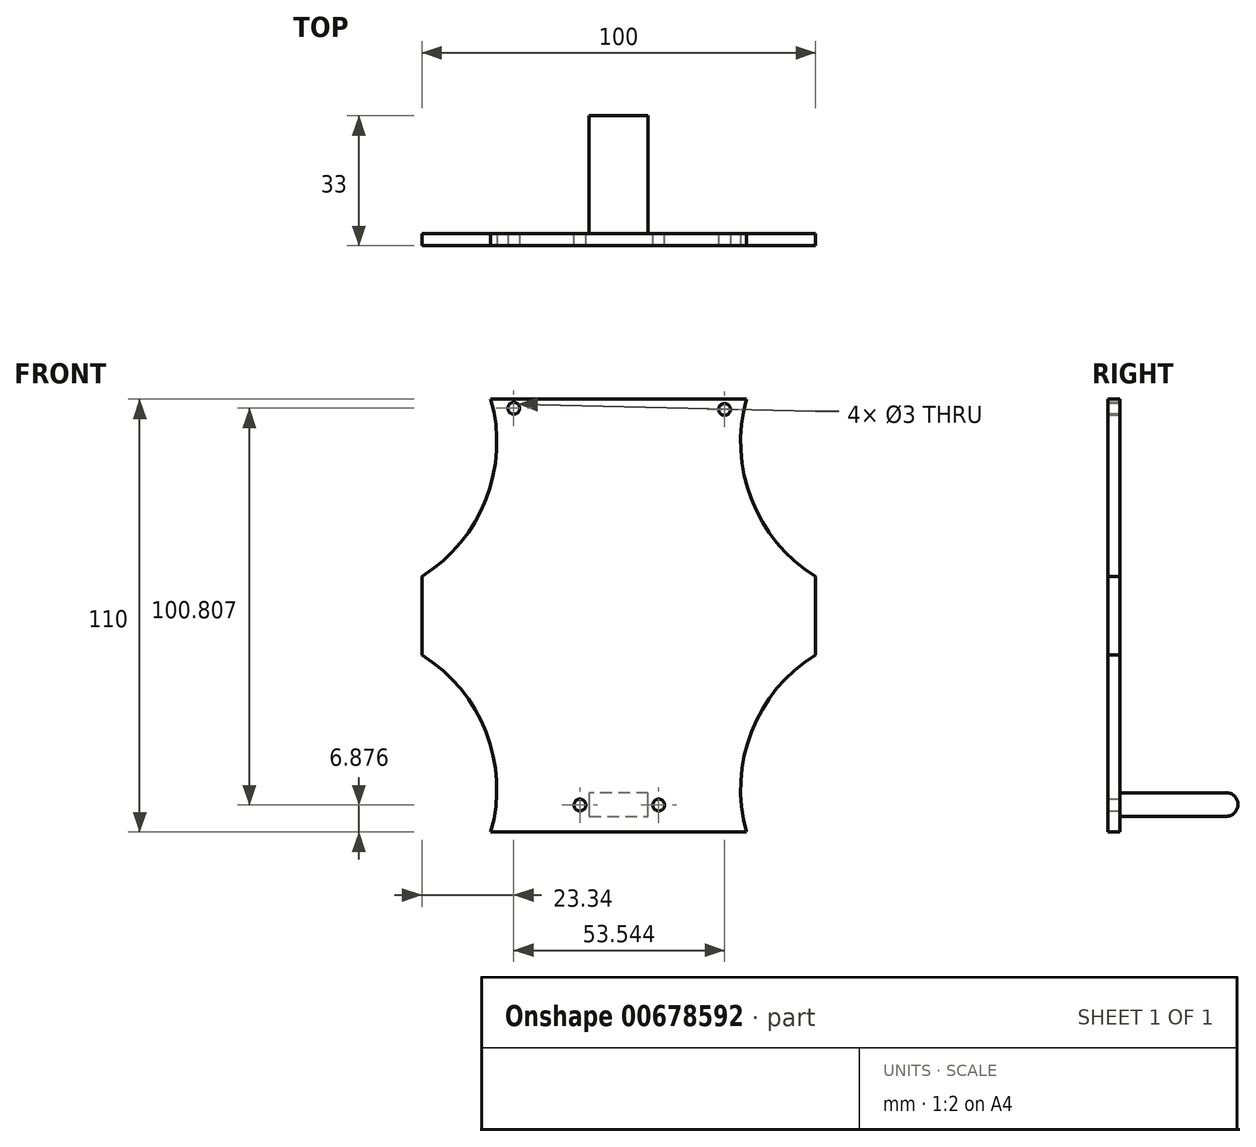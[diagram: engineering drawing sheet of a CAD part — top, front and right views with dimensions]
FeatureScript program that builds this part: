
annotation { "Feature Type Name" : "Feature", "Feature Type Description" : "" }
export const myFeature = defineFeature(function(context is Context, id is Id, definition is map)
    precondition{}
    {
        {
            var Q0;
            Q0=qCreatedBy(makeId("Front.planeOp"),FACE);
            var sketch = newSketch(context, id + "F0", { "sketchPlane" : qUnion([Q0])});
            skLineSegment(sketch, "E0.bottom", {"start": v(0, 0) * mm, "end": v(100, 0) * mm});
            skLineSegment(sketch, "E0.top", {"start": v(0, 110) * mm, "end": v(100, 110) * mm});
            skLineSegment(sketch, "E0.left", {"start": v(0, 0) * mm, "end": v(0, 110) * mm});
            skLineSegment(sketch, "E0.right", {"start": v(100, 0) * mm, "end": v(100, 110) * mm});
            skSolve(sketch);
        }
        {
            var Q0;
            Q0=makeQuery(id+"F0.imprint","IMPRINT",FACE,{"disambiguationData":[TD([[makeQuery(id+"F0.imprint","IMPRINT",EDGE,{"derivedFrom":sQuery(id+"F0.wireOp",EDGE,"E0.bottom")}),1.0]])]});
            extrude(context, id + "F1", {"entities" : qUnion([Q0]), "depth" : 3 * mm, "offsetDistance" : 25 * mm});
        }
        {
            var Q0;
            Q0=makeQuery(id+"F1.opExtrude","CAP_FACE",FACE,{"disambiguationData":[OSD([sQuery(id+"F0.wireOp",EDGE,"E0.bottom"),sQuery(id+"F0.wireOp",EDGE,"E0.top"),sQuery(id+"F0.wireOp",EDGE,"E0.left"),sQuery(id+"F0.wireOp",EDGE,"E0.right")])],"isStart":false});
            var sketch = newSketch(context, id + "F2", { "sketchPlane" : qUnion([Q0])});
            skLineSegment(sketch, "E1", {"start": v(0, 0) * mm, "end": v(0, 45) * mm});
            skLineSegment(sketch, "E2", {"start": v(0, 110) * mm, "end": v(0, 65) * mm});
            skLineSegment(sketch, "E3", {"start": v(100, 110) * mm, "end": v(100, 65) * mm});
            skLineSegment(sketch, "E4", {"start": v(100, 0) * mm, "end": v(100, 45) * mm});
            skLineSegment(sketch, "E5", {"start": v(0, 0) * mm, "end": v(17.5, 0) * mm});
            skLineSegment(sketch, "E6", {"start": v(100, 0) * mm, "end": v(82.5, 0) * mm});
            skLineSegment(sketch, "E7", {"start": v(0, 110) * mm, "end": v(17.5, 110) * mm});
            skLineSegment(sketch, "E8", {"start": v(100, 110) * mm, "end": v(82.5, 110) * mm});
            skArc(sketch, "E9", {"start": v(0, 65) * mm, "mid": v(16.3, 84.56) * mm, "end": v(17.5, 110) * mm});
            skArc(sketch, "E10", {"start": v(82.5, 110) * mm, "mid": v(83.7, 84.56) * mm, "end": v(100, 65) * mm});
            skArc(sketch, "E11", {"start": v(100, 45) * mm, "mid": v(83.7, 25.44) * mm, "end": v(82.5, 0) * mm});
            skArc(sketch, "E12", {"start": v(17.5, 0) * mm, "mid": v(16.3, 25.44) * mm, "end": v(0, 45) * mm});
            skSolve(sketch);
        }
        {
            var Q0;
            Q0=makeQuery(id+"F2.imprint","IMPRINT",FACE,{"disambiguationData":[TD([[makeQuery(id+"F2.imprint","IMPRINT",EDGE,{"derivedFrom":sQuery(id+"F2.wireOp",EDGE,"E2")}),-1.0]])]});
            var Q1;
            Q1=makeQuery(id+"F2.imprint","IMPRINT",FACE,{"disambiguationData":[TD([[makeQuery(id+"F2.imprint","IMPRINT",EDGE,{"derivedFrom":sQuery(id+"F2.wireOp",EDGE,"E3")}),1.0]])]});
            var Q2;
            Q2=makeQuery(id+"F2.imprint","IMPRINT",FACE,{"disambiguationData":[TD([[makeQuery(id+"F2.imprint","IMPRINT",EDGE,{"derivedFrom":sQuery(id+"F2.wireOp",EDGE,"E4")}),1.0]])]});
            var Q3;
            Q3=makeQuery(id+"F2.imprint","IMPRINT",FACE,{"disambiguationData":[TD([[makeQuery(id+"F2.imprint","IMPRINT",EDGE,{"derivedFrom":sQuery(id+"F2.wireOp",EDGE,"E1")}),-1.0]])]});
            extrude(context, id + "F3", {"entities" : qUnion([Q0, Q1, Q2, Q3]), "operationType" : NewBodyOperationType.REMOVE, "oppositeDirection" : true, "depth" : 25 * mm, "offsetDistance" : 25 * mm});
        }
        {
            var Q0;
            Q0=makeQuery(id+"F1.opExtrude","CAP_FACE",FACE,{"disambiguationData":[OSD([sQuery(id+"F0.wireOp",EDGE,"E0.bottom"),sQuery(id+"F0.wireOp",EDGE,"E0.top"),sQuery(id+"F0.wireOp",EDGE,"E0.left"),sQuery(id+"F0.wireOp",EDGE,"E0.right")])],"isStart":true});
            var sketch = newSketch(context, id + "F4", { "sketchPlane" : qUnion([Q0])});
            skLineSegment(sketch, "E13", {"start": v(-82.5, 0) * mm, "end": v(-57.5, 0) * mm});
            skLineSegment(sketch, "E14", {"start": v(-17.5, 0) * mm, "end": v(-42.5, 0) * mm});
            skLineSegment(sketch, "E15", {"start": v(-42.5, 4) * mm, "end": v(-57.5, 4) * mm});
            skLineSegment(sketch, "E16", {"start": v(-57.5, 4) * mm, "end": v(-57.5, 10) * mm});
            skLineSegment(sketch, "E17", {"start": v(-57.5, 10) * mm, "end": v(-42.5, 10) * mm});
            skLineSegment(sketch, "E18", {"start": v(-42.5, 10) * mm, "end": v(-42.5, 4) * mm});
            skSolve(sketch);
        }
        {
            var Q0;
            Q0=makeQuery(id+"F4.imprint","IMPRINT",FACE,{"disambiguationData":[TD([[makeQuery(id+"F4.imprint","IMPRINT",EDGE,{"derivedFrom":sQuery(id+"F4.wireOp",EDGE,"E15")}),-1.0]])]});
            extrude(context, id + "F5", {"entities" : qUnion([Q0]), "operationType" : NewBodyOperationType.ADD, "depth" : 30 * mm, "offsetDistance" : 25 * mm});
        }
        {
            var Q0;
            Q0=makeQuery(id+"F5.opExtrude","CAP_EDGE",EDGE,{"disambiguationData":[OSD([sQuery(id+"F4.wireOp",EDGE,"E15")])],"isStart":false});
            fillet(context, id + "F6", {"entities" : qUnion([Q0]), "radius" : 3 * mm, "tangentPropagation" : true, "allowEdgeOverflow" : false});
        }
        {
            var Q0;
            Q0=makeQuery(id+"F5.opExtrude","CAP_EDGE",EDGE,{"disambiguationData":[OSD([sQuery(id+"F4.wireOp",EDGE,"E17")])],"isStart":false});
            fillet(context, id + "F7", {"entities" : qUnion([Q0]), "radius" : 3 * mm, "tangentPropagation" : true, "allowEdgeOverflow" : false});
        }
        {
            var Q0;
            Q0=makeQuery(id+"F1.opExtrude","CAP_FACE",FACE,{"disambiguationData":[OSD([sQuery(id+"F0.wireOp",EDGE,"E0.bottom"),sQuery(id+"F0.wireOp",EDGE,"E0.top"),sQuery(id+"F0.wireOp",EDGE,"E0.left"),sQuery(id+"F0.wireOp",EDGE,"E0.right")])],"isStart":true});
            var sketch = newSketch(context, id + "F8", { "sketchPlane" : qUnion([Q0])});
            skCircle(sketch, "E19", {"center": v(-40.15, 6.88) * mm, "radius": 1.5 * mm});
            skCircle(sketch, "E20", {"center": v(-60.15, 6.88) * mm, "radius": 1.5 * mm});
            skSolve(sketch);
        }
        {
            var Q0;
            Q0=makeQuery(id+"F8.imprint","IMPRINT",FACE,{"disambiguationData":[TD([[makeQuery(id+"F8.imprint","IMPRINT",EDGE,{"derivedFrom":sQuery(id+"F8.wireOp",EDGE,"E19")}),1.0]])]});
            var Q1;
            Q1=makeQuery(id+"F8.imprint","IMPRINT",FACE,{"disambiguationData":[TD([[makeQuery(id+"F8.imprint","IMPRINT",EDGE,{"derivedFrom":sQuery(id+"F8.wireOp",EDGE,"E20")}),1.0]])]});
            extrude(context, id + "F9", {"entities" : qUnion([Q0, Q1]), "operationType" : NewBodyOperationType.REMOVE, "oppositeDirection" : true, "depth" : 25 * mm, "offsetDistance" : 25 * mm});
        }
        {
            var Q0;
            Q0=makeQuery(id+"F1.opExtrude","CAP_FACE",FACE,{"disambiguationData":[OSD([sQuery(id+"F0.wireOp",EDGE,"E0.bottom"),sQuery(id+"F0.wireOp",EDGE,"E0.top"),sQuery(id+"F0.wireOp",EDGE,"E0.left"),sQuery(id+"F0.wireOp",EDGE,"E0.right")])],"isStart":false});
            var sketch = newSketch(context, id + "F10", { "sketchPlane" : qUnion([Q0])});
            skCircle(sketch, "E21", {"center": v(23.34, 107.68) * mm, "radius": 1.5 * mm});
            skCircle(sketch, "E22", {"center": v(76.88, 107.37) * mm, "radius": 1.5 * mm});
            skSolve(sketch);
        }
        {
            var Q0;
            Q0=makeQuery(id+"F10.imprint","IMPRINT",FACE,{"disambiguationData":[TD([[makeQuery(id+"F10.imprint","IMPRINT",EDGE,{"derivedFrom":sQuery(id+"F10.wireOp",EDGE,"E21")}),1.0]])]});
            var Q1;
            Q1=makeQuery(id+"F10.imprint","IMPRINT",FACE,{"disambiguationData":[TD([[makeQuery(id+"F10.imprint","IMPRINT",EDGE,{"derivedFrom":sQuery(id+"F10.wireOp",EDGE,"E22")}),1.0]])]});
            extrude(context, id + "F11", {"entities" : qUnion([Q0, Q1]), "operationType" : NewBodyOperationType.REMOVE, "oppositeDirection" : true, "depth" : 25 * mm, "offsetDistance" : 25 * mm});
        }
    });
